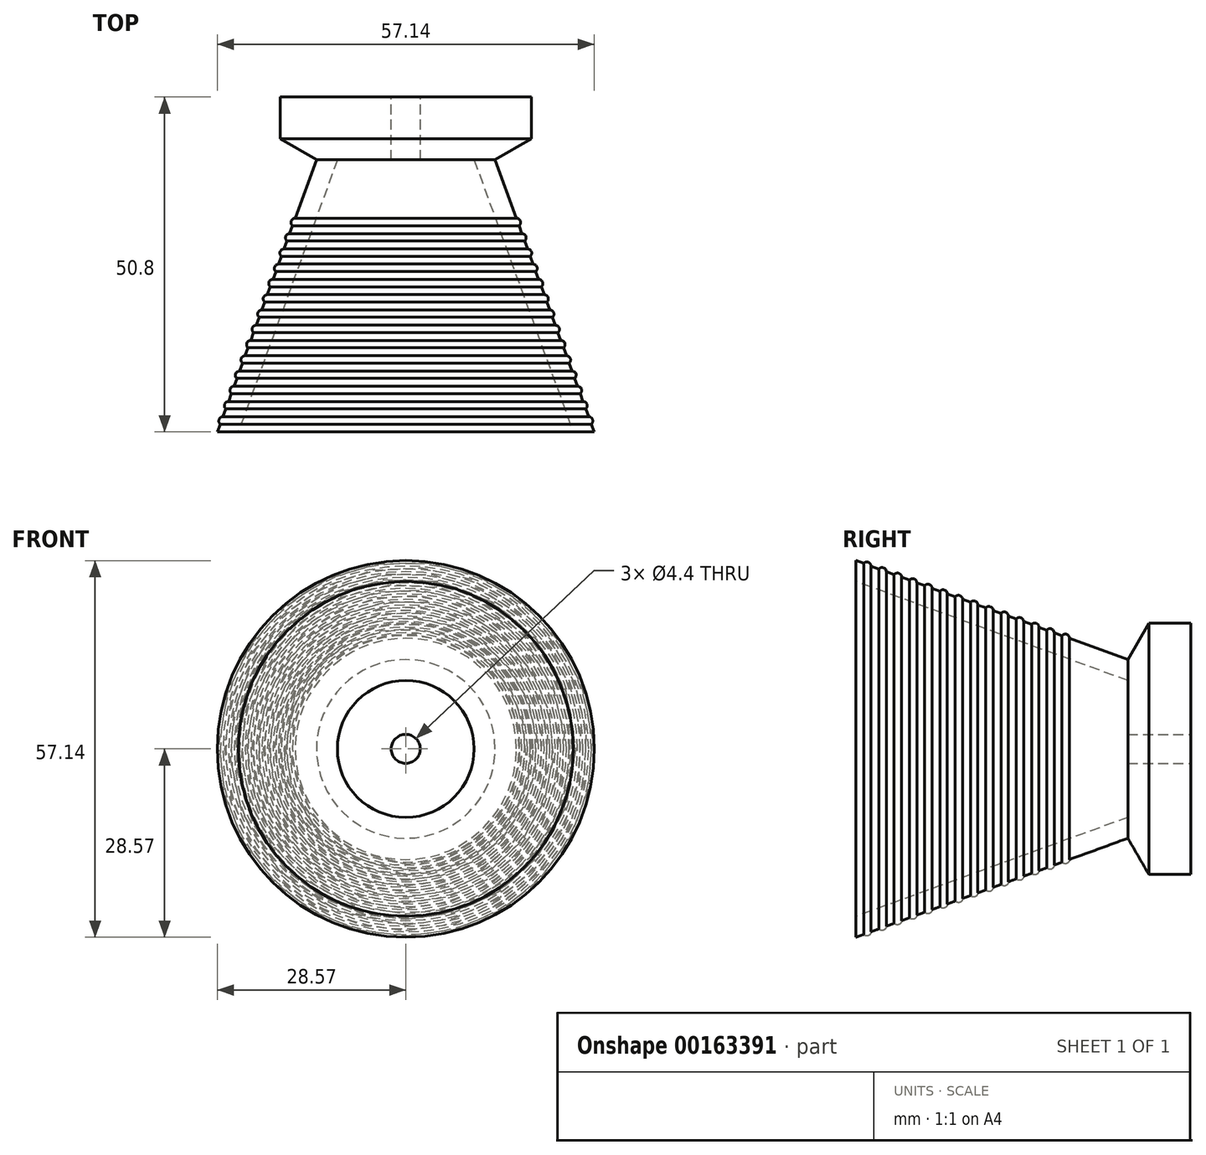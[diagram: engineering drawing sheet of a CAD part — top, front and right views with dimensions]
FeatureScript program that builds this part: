
annotation { "Feature Type Name" : "Feature", "Feature Type Description" : "" }
export const myFeature = defineFeature(function(context is Context, id is Id, definition is map)
    precondition{}
    {
        {
            var Q0;
            Q0=qCreatedBy(makeId("Right.planeOp"),FACE);
            var sketch = newSketch(context, id + "F0", { "sketchPlane" : qUnion([Q0])});
            skLineSegment(sketch, "E0", {"start": v(0, 19.05) * mm, "end": v(-2.54, 19.05) * mm});
            skLineSegment(sketch, "E1", {"start": v(-2.54, 19.05) * mm, "end": v(-2.54, 19.05) * mm});
            skLineSegment(sketch, "E2", {"start": v(-2.54, 19.05) * mm, "end": v(-5.08, 19.05) * mm});
            skLineSegment(sketch, "E3", {"start": v(-5.08, 19.05) * mm, "end": v(-5.08, 19.05) * mm});
            skLineSegment(sketch, "E4", {"start": v(-5.08, 19.05) * mm, "end": v(-6.35, 19.05) * mm});
            skLineSegment(sketch, "E5", {"start": v(-6.35, 19.05) * mm, "end": v(-9.52, 13.55) * mm});
            skLineSegment(sketch, "E6", {"start": v(-9.52, 13.55) * mm, "end": v(-18.4, 16.78) * mm});
            skLineSegment(sketch, "E7", {"start": v(-50.8, 28.57) * mm, "end": v(-50.8, 25.4) * mm});
            skLineSegment(sketch, "E8", {"start": v(0, 19.05) * mm, "end": v(0, 0) * mm});
            skArc(sketch, "E9", {"start": v(-48.49, 27.73) * mm, "mid": v(-48.9, 28.33) * mm, "end": v(-49.6, 28.14) * mm});
            skLineSegment(sketch, "E10.trimOffspring", {"start": v(-49.6, 28.14) * mm, "end": v(-50.8, 28.57) * mm});
            skArc(sketch, "E11", {"start": v(-46.17, 26.89) * mm, "mid": v(-46.59, 27.49) * mm, "end": v(-47.3, 27.3) * mm});
            skArc(sketch, "E12", {"start": v(-43.86, 26.05) * mm, "mid": v(-44.27, 26.64) * mm, "end": v(-44.98, 26.45) * mm});
            skArc(sketch, "E13", {"start": v(-41.54, 25.2) * mm, "mid": v(-41.96, 25.8) * mm, "end": v(-42.66, 25.61) * mm});
            skArc(sketch, "E14", {"start": v(-39.23, 24.36) * mm, "mid": v(-39.64, 24.96) * mm, "end": v(-40.35, 24.77) * mm});
            skArc(sketch, "E15", {"start": v(-36.91, 23.52) * mm, "mid": v(-37.33, 24.12) * mm, "end": v(-38.03, 23.93) * mm});
            skArc(sketch, "E16", {"start": v(-34.6, 22.68) * mm, "mid": v(-35.01, 23.27) * mm, "end": v(-35.72, 23.08) * mm});
            skArc(sketch, "E17", {"start": v(-32.28, 21.83) * mm, "mid": v(-32.7, 22.43) * mm, "end": v(-33.4, 22.24) * mm});
            skArc(sketch, "E18", {"start": v(-29.97, 21) * mm, "mid": v(-30.38, 21.59) * mm, "end": v(-31.09, 21.4) * mm});
            skArc(sketch, "E19", {"start": v(-27.65, 20.15) * mm, "mid": v(-28.07, 20.74) * mm, "end": v(-28.77, 20.56) * mm});
            skArc(sketch, "E20", {"start": v(-25.34, 19.3) * mm, "mid": v(-25.75, 19.9) * mm, "end": v(-26.46, 19.71) * mm});
            skArc(sketch, "E21", {"start": v(-23.02, 18.46) * mm, "mid": v(-23.44, 19.06) * mm, "end": v(-24.14, 18.87) * mm});
            skArc(sketch, "E22", {"start": v(-20.7, 17.62) * mm, "mid": v(-21.12, 18.22) * mm, "end": v(-21.83, 18.03) * mm});
            skArc(sketch, "E23", {"start": v(-18.4, 16.78) * mm, "mid": v(-18.8, 17.37) * mm, "end": v(-19.51, 17.19) * mm});
            skLineSegment(sketch, "E24.trimOffspring", {"start": v(-47.3, 27.3) * mm, "end": v(-48.49, 27.73) * mm});
            skLineSegment(sketch, "E25.trimOffspring", {"start": v(-44.98, 26.45) * mm, "end": v(-46.17, 26.89) * mm});
            skLineSegment(sketch, "E26.trimOffspring", {"start": v(-42.66, 25.61) * mm, "end": v(-43.86, 26.05) * mm});
            skLineSegment(sketch, "E27.trimOffspring", {"start": v(-19.51, 17.19) * mm, "end": v(-20.7, 17.62) * mm});
            skLineSegment(sketch, "E28.trimOffspring", {"start": v(-21.83, 18.03) * mm, "end": v(-23.02, 18.46) * mm});
            skLineSegment(sketch, "E29.trimOffspring", {"start": v(-24.14, 18.87) * mm, "end": v(-25.34, 19.3) * mm});
            skLineSegment(sketch, "E30.trimOffspring", {"start": v(-26.46, 19.71) * mm, "end": v(-27.65, 20.15) * mm});
            skLineSegment(sketch, "E31.trimOffspring", {"start": v(-28.77, 20.56) * mm, "end": v(-29.97, 21) * mm});
            skLineSegment(sketch, "E32.trimOffspring", {"start": v(-31.09, 21.4) * mm, "end": v(-32.28, 21.83) * mm});
            skLineSegment(sketch, "E33.trimOffspring", {"start": v(-33.4, 22.24) * mm, "end": v(-34.6, 22.68) * mm});
            skLineSegment(sketch, "E34.trimOffspring", {"start": v(-35.72, 23.08) * mm, "end": v(-36.91, 23.52) * mm});
            skLineSegment(sketch, "E35.trimOffspring", {"start": v(-38.03, 23.93) * mm, "end": v(-39.23, 24.36) * mm});
            skLineSegment(sketch, "E36.trimOffspring", {"start": v(-40.35, 24.77) * mm, "end": v(-41.54, 25.2) * mm});
            skLineSegment(sketch, "E37", {"start": v(-50.8, 25.4) * mm, "end": v(-9.52, 10.38) * mm});
            skLineSegment(sketch, "E38", {"start": v(-9.52, 10.38) * mm, "end": v(-9.52, 0) * mm});
            skLineSegment(sketch, "E39", {"start": v(-9.52, 0) * mm, "end": v(0, 0) * mm});
            skSolve(sketch);
        }
        {
            var Q0;
            Q0=qCreatedBy(makeId("Right.planeOp"),FACE);
            var sketch = newSketch(context, id + "F1", { "sketchPlane" : qUnion([Q0])});
            skLineSegment(sketch, "E40", {"start": v(-57.7, 0) * mm, "end": v(0, 0) * mm, "construction": true});
            skSolve(sketch);
        }
        {
            var Q0;
            Q0 = qSketchRegion(id + "F0", true);
            var Q1;
            Q1 = qConstructionFilter(qBodyType(qCreatedBy(id + "F0" ,EDGE), BodyType.WIRE), ConstructionObject.NO);
            var Q2;
            Q2=sQuery(id+"F1.wireOp",EDGE,"E40");
            revolve(context, id + "F2", {"entities" : qUnion([Q0]), "surfaceEntities" : qUnion([Q1]), "axis" : qUnion([Q2]), "revolveType" : RevolveType.FULL});
        }
        {
            var Q0;
            Q0=makeQuery(id+"F2.opRevolve","SWEPT_FACE",FACE,{"disambiguationData":[OSD([sQuery(id+"F0.wireOp",EDGE,"E8")])]});
            var sketch = newSketch(context, id + "F3", { "sketchPlane" : qUnion([Q0])});
            skPoint(sketch, "E41", {"position": v(0, 0) * mm});
            skSolve(sketch);
        }
        {
            var Q0;
            Q0=sQuery(id+"F3.wireOp",VERTEX,"E41");
            var Q1;
            Q1=makeQuery(id+"F2.opRevolve","SWEPT_BODY",BODY,{"disambiguationData":[OSD([sQuery(id+"F0.wireOp",EDGE,"E0"),sQuery(id+"F0.wireOp",EDGE,"E1"),sQuery(id+"F0.wireOp",EDGE,"E2"),sQuery(id+"F0.wireOp",EDGE,"E3"),sQuery(id+"F0.wireOp",EDGE,"E4"),sQuery(id+"F0.wireOp",EDGE,"E5"),sQuery(id+"F0.wireOp",EDGE,"E6"),sQuery(id+"F0.wireOp",EDGE,"E7"),sQuery(id+"F0.wireOp",EDGE,"E8"),sQuery(id+"F0.wireOp",EDGE,"E9"),sQuery(id+"F0.wireOp",EDGE,"E10.trimOffspring"),sQuery(id+"F0.wireOp",EDGE,"E11"),sQuery(id+"F0.wireOp",EDGE,"E12"),sQuery(id+"F0.wireOp",EDGE,"E13"),sQuery(id+"F0.wireOp",EDGE,"E14"),sQuery(id+"F0.wireOp",EDGE,"E15"),sQuery(id+"F0.wireOp",EDGE,"E16"),sQuery(id+"F0.wireOp",EDGE,"E17"),sQuery(id+"F0.wireOp",EDGE,"E18"),sQuery(id+"F0.wireOp",EDGE,"E19"),sQuery(id+"F0.wireOp",EDGE,"E20"),sQuery(id+"F0.wireOp",EDGE,"E21"),sQuery(id+"F0.wireOp",EDGE,"E22"),sQuery(id+"F0.wireOp",EDGE,"E23"),sQuery(id+"F0.wireOp",EDGE,"E24.trimOffspring"),sQuery(id+"F0.wireOp",EDGE,"E25.trimOffspring"),sQuery(id+"F0.wireOp",EDGE,"E26.trimOffspring"),sQuery(id+"F0.wireOp",EDGE,"E27.trimOffspring"),sQuery(id+"F0.wireOp",EDGE,"E28.trimOffspring"),sQuery(id+"F0.wireOp",EDGE,"E29.trimOffspring"),sQuery(id+"F0.wireOp",EDGE,"E30.trimOffspring"),sQuery(id+"F0.wireOp",EDGE,"E31.trimOffspring"),sQuery(id+"F0.wireOp",EDGE,"E32.trimOffspring"),sQuery(id+"F0.wireOp",EDGE,"E33.trimOffspring"),sQuery(id+"F0.wireOp",EDGE,"E34.trimOffspring"),sQuery(id+"F0.wireOp",EDGE,"E35.trimOffspring"),sQuery(id+"F0.wireOp",EDGE,"E36.trimOffspring"),sQuery(id+"F0.wireOp",EDGE,"E37"),sQuery(id+"F0.wireOp",EDGE,"E38"),sQuery(id+"F0.wireOp",EDGE,"E39")])]});
            hole(context, id + "F4", {"style" : HoleStyle.SIMPLE, "endStyle" : HoleEndStyle.THROUGH, "standardTappedOrClearance" : lookupTablePath({ "standard" : "ISO", "fit" : "Normal", "size" : "M4", "type" : "Clearance" }), "standardBlindInLast" : lookupTablePath({ "fit" : "Standard", "standard" : "ISO", "size" : "M4", "type" : "Clearance" }), "holeDiameter" : 4.4 * mm, "locations" : qUnion([Q0]), "scope" : qUnion([Q1]), "isTappedThrough" : true});
        }
    });
